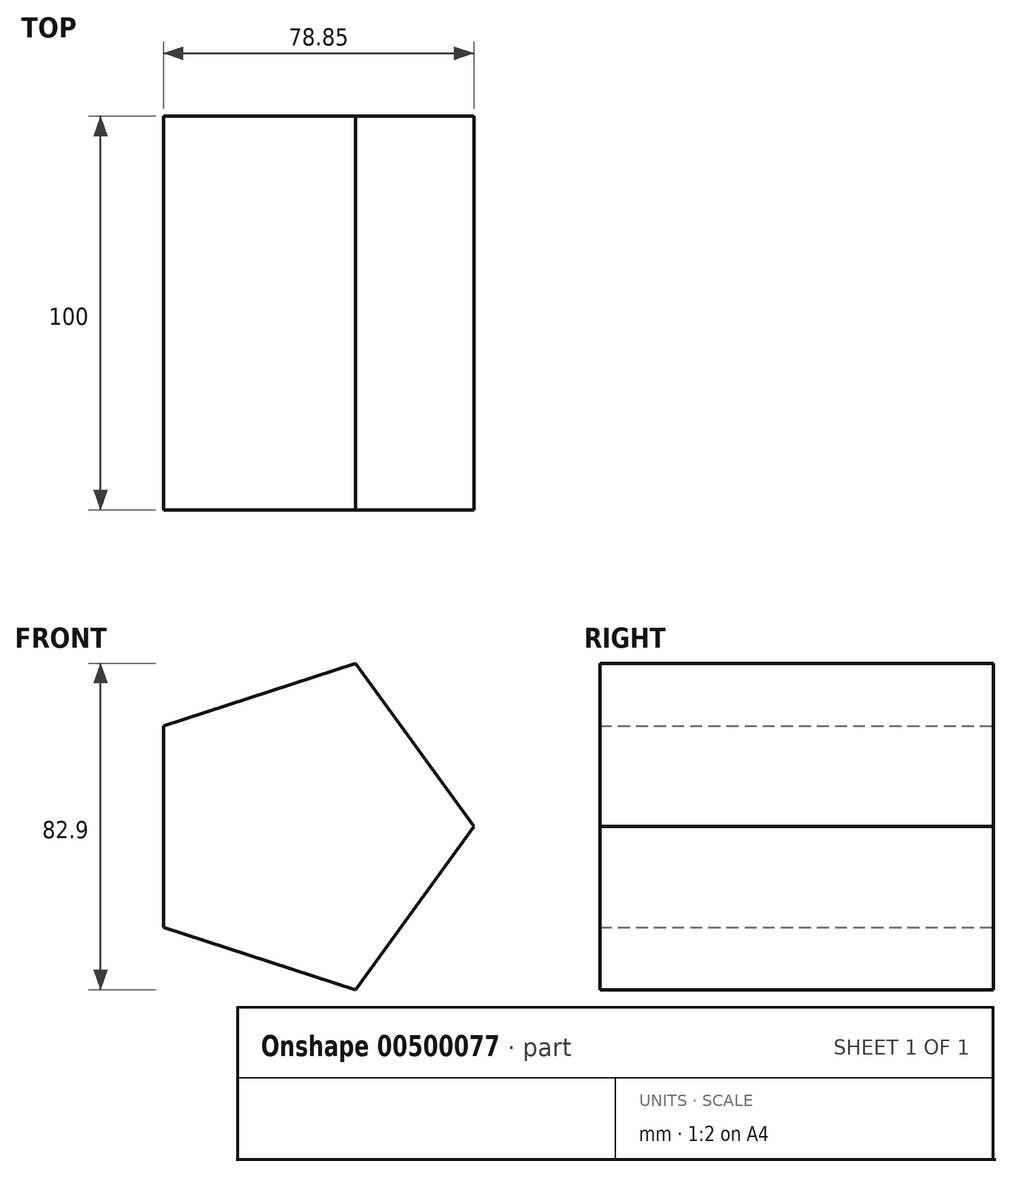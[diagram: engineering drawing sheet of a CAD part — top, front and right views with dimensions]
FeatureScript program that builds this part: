
annotation { "Feature Type Name" : "Feature", "Feature Type Description" : "" }
export const myFeature = defineFeature(function(context is Context, id is Id, definition is map)
    precondition{}
    {
        {
            var Q0;
            Q0=qCreatedBy(makeId("Front.planeOp"),FACE);
            var sketch = newSketch(context, id + "F0", { "sketchPlane" : qUnion([Q0])});
            skCircle(sketch, "E0.cCircle", {"center": v(0, 0) * mm, "radius": 43.59 * mm, "construction": true});
            skLineSegment(sketch, "E0.0", {"start": v(43.59, 0) * mm, "end": v(13.47, -41.45) * mm});
            skLineSegment(sketch, "E0.1", {"start": v(13.47, -41.45) * mm, "end": v(-35.26, -25.62) * mm});
            skLineSegment(sketch, "E0.2", {"start": v(-35.26, -25.62) * mm, "end": v(-35.26, 25.62) * mm});
            skLineSegment(sketch, "E0.3", {"start": v(-35.26, 25.62) * mm, "end": v(13.47, 41.45) * mm});
            skLineSegment(sketch, "E0.4", {"start": v(13.47, 41.45) * mm, "end": v(43.59, 0) * mm});
            skSolve(sketch);
        }
        {
            var Q0;
            Q0=makeQuery(id+"F0.imprint","IMPRINT",FACE,{"disambiguationData":[TD([[makeQuery(id+"F0.imprint","IMPRINT",EDGE,{"derivedFrom":sQuery(id+"F0.wireOp",EDGE,"E0.0")}),-1.0]])]});
            extrude(context, id + "F1", {"entities" : qUnion([Q0]), "endBound" : BoundingType.SYMMETRIC, "depth" : 100 * mm});
        }
    });
